# Revit family: Foundation-Barrier-Pango-Claw_Tape
name_source: partatom
category: Specialty Equipment
units: mm (PartAtom-declared; Revit-internal decimal feet)

## family parameters
Cut with Voids When Loaded = No
Host = Face
OmniClass Number = 23.25.05.21
OmniClass Title = Special Foundations
Part Type = Normal
Room Calculation Point = No
Round Connector Dimension = Use Diameter
Shared = No

## types (1)
- Pango Claw® 3" Wide
    BIMobject category = Waterproofing & Membranes
Waterproofing & Membranes
    Brand url = http://www.stegoindustries.com
    Crete Claw Depth = 0' - 3"
    Date of publishing = 8/16/2017
    Default Elevation = 0' - 0"
    Description = multi-layered tape that is used to seal Pango Wrap along its terminating edges (interior and perimeter) to the slab. Pango Claw allows wet concrete to cast into the textured top surface to form a mechanical bond/seal. Made from the same uniquely designed barrier technology as Pango Wrap, it is a physical barrier to subterranean termites and an ideal accessory for completing a fully intaact, monolithic Pango Wrap installation.
    Design country = United States
    Edition number = 1
    Height = 1' - 7"
    Installation instructions = https://www.stegoindustries.com
    Low Emitting Material = Yes
    Manufacturer = Stego Industries, LLC
    Manufacturer country = United States
    Manufacturer name = Stego Industries, LLC
    Masterformat 2014 Code = 07 26 00
    Masterformat 2014 Description = Vapor Retarders
    Material main = Polyethylene
    Material secondary = Acrylic
    Max Length Note = Pango Claw® is available in rolls of 180'.
    Model = Pango Claw® 3" wide
    Nominal height = 0' - 0"
    Nominal width = 0' - 0"
    Product Guid = https://www.stegoindustries.com
    Product Page URL = https://www.stegoindustries.com
    Product SKU = stego010
stego010
stego010
stego010
    Product certification = https://www.stegoindustries.com
https://www.stegoindustries.com
    Product data url = https://bimobject.com
    Product family = Thermal and Moisture Protective Products / Pango Wrap Termite and Vapor Barrier
    Product group = Pango Wrap Vapor & Termite Barrier
    Product url = https://www.stegoindustries.com
    QR code = https://bimobject.com
https://bimobject.com
    Stego Crete Claw = Pango Claw® Tape
    Technical description = multi-layered tape that is used to seal Pango Wrap along its terminating edges (interior and perimeter) to the slab.
    Thickness = 0' - 0 1/16"
    URL = https://www.stegoindustries.com
    Weight Net (Kg) = 0
    Youtube clip = https://www.youtube.com

## geometry (parser evidence)
native form markers: Sweep x3
no freeform markers — native parametric forms only
